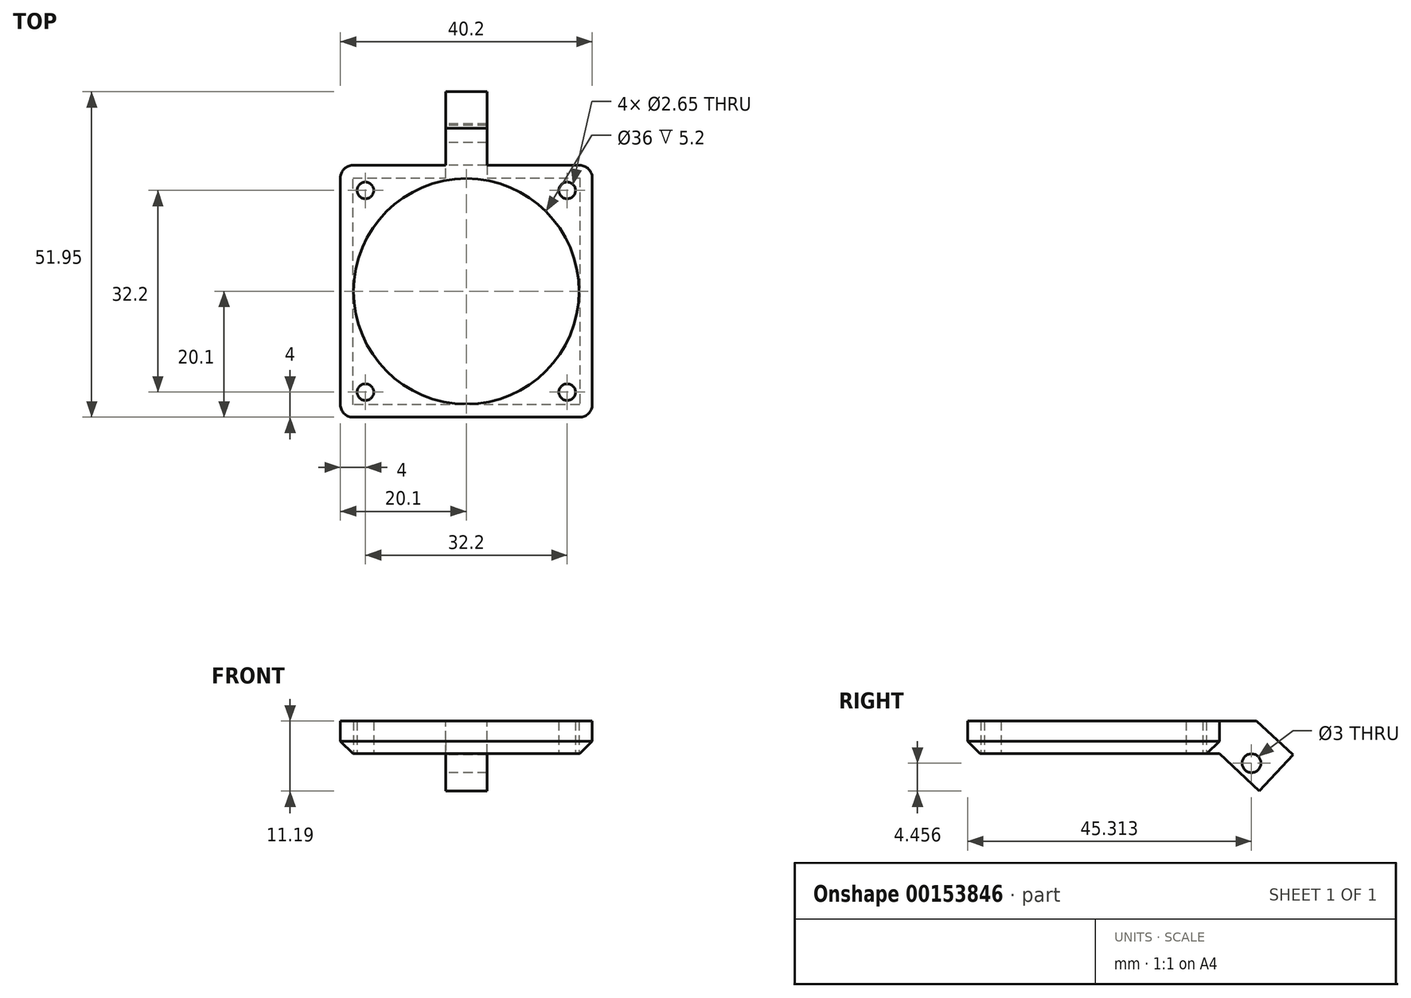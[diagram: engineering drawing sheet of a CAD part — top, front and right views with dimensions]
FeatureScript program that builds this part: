
annotation { "Feature Type Name" : "Feature", "Feature Type Description" : "" }
export const myFeature = defineFeature(function(context is Context, id is Id, definition is map)
    precondition{}
    {
        {
            var Q0;
            Q0=qCreatedBy(makeId("Top.planeOp"),FACE);
            var sketch = newSketch(context, id + "F0", { "sketchPlane" : qUnion([Q0])});
            skLineSegment(sketch, "E0.bottom", {"start": v(20.1, -20.1) * mm, "end": v(-20.1, -20.1) * mm});
            skLineSegment(sketch, "E0.top", {"start": v(20.1, 20.1) * mm, "end": v(-20.1, 20.1) * mm});
            skLineSegment(sketch, "E0.left", {"start": v(20.1, -20.1) * mm, "end": v(20.1, 20.1) * mm});
            skLineSegment(sketch, "E0.right", {"start": v(-20.1, -20.1) * mm, "end": v(-20.1, 20.1) * mm});
            skPoint(sketch, "E0.middle", {"position": v(0, 0) * mm});
            skLineSegment(sketch, "E1.bottom", {"start": v(-20.1, 20.1) * mm, "end": v(-16.1, 20.1) * mm, "construction": true});
            skLineSegment(sketch, "E1.top", {"start": v(-20.1, 16.1) * mm, "end": v(-16.1, 16.1) * mm, "construction": true});
            skLineSegment(sketch, "E1.left", {"start": v(-20.1, 20.1) * mm, "end": v(-20.1, 16.1) * mm, "construction": true});
            skLineSegment(sketch, "E1.right", {"start": v(-16.1, 20.1) * mm, "end": v(-16.1, 16.1) * mm, "construction": true});
            skCircle(sketch, "E2", {"center": v(-16.1, 16.1) * mm, "radius": 1.32 * mm});
            skCircle(sketch, "E3.1.0.0", {"center": v(16.1, 16.1) * mm, "radius": 1.32 * mm});
            skLineSegment(sketch, "E3.direction1", {"start": v(-16.1, 16.1) * mm, "end": v(16.1, 16.1) * mm, "construction": true});
            skLineSegment(sketch, "E4.MirrorCS", {"start": v(-20.1, -20.1) * mm, "end": v(-16.1, -20.1) * mm, "construction": true});
            skLineSegment(sketch, "E5.MirrorCS", {"start": v(-20.1, -16.1) * mm, "end": v(-16.1, -16.1) * mm, "construction": true});
            skLineSegment(sketch, "E6.MirrorCS", {"start": v(-16.1, -20.1) * mm, "end": v(-16.1, -16.1) * mm, "construction": true});
            skLineSegment(sketch, "E7.MirrorCS", {"start": v(-20.1, -20.1) * mm, "end": v(-20.1, -16.1) * mm, "construction": true});
            skLineSegment(sketch, "E8.MirrorCS", {"start": v(-16.1, -16.1) * mm, "end": v(16.1, -16.1) * mm, "construction": true});
            skCircle(sketch, "E9.MirrorC", {"center": v(-16.1, -16.1) * mm, "radius": 1.32 * mm});
            skCircle(sketch, "E10.MirrorC", {"center": v(16.1, -16.1) * mm, "radius": 1.32 * mm});
            skCircle(sketch, "E11", {"center": v(0, 0) * mm, "radius": 18 * mm});
            skCircle(sketch, "E12", {"center": v(6.17, 0) * mm, "radius": 0.24 * mm});
            skSolve(sketch);
        }
        {
            var Q0;
            Q0=makeQuery(id+"F0.imprint","IMPRINT",FACE,{"disambiguationData":[TD([[makeQuery(id+"F0.imprint","IMPRINT",EDGE,{"derivedFrom":sQuery(id+"F0.wireOp",EDGE,"E0.top")}),1.0]])]});
            extrude(context, id + "F1", {"entities" : qUnion([Q0]), "depth" : 5.2 * mm});
        }
        {
            var Q0;
            Q0=makeQuery(id+"F1.opExtrude","SWEPT_EDGE",EDGE,{"disambiguationData":[OSD([sQuery(id+"F0.wireOp",EDGE,"E0.top"),sQuery(id+"F0.wireOp",EDGE,"E0.right")])]});
            var Q1;
            Q1=makeQuery(id+"F1.opExtrude","SWEPT_EDGE",EDGE,{"disambiguationData":[OSD([sQuery(id+"F0.wireOp",EDGE,"E0.top"),sQuery(id+"F0.wireOp",EDGE,"E0.left")])]});
            var Q2;
            Q2=makeQuery(id+"F1.opExtrude","SWEPT_EDGE",EDGE,{"disambiguationData":[OSD([sQuery(id+"F0.wireOp",EDGE,"E0.left"),sQuery(id+"F0.wireOp",EDGE,"E0.bottom")])]});
            var Q3;
            Q3=makeQuery(id+"F1.opExtrude","SWEPT_EDGE",EDGE,{"disambiguationData":[OSD([sQuery(id+"F0.wireOp",EDGE,"E0.right"),sQuery(id+"F0.wireOp",EDGE,"E0.bottom")])]});
            fillet(context, id + "F2", {"entities" : qUnion([Q0, Q1, Q2, Q3]), "radius" : 2 * mm, "tangentPropagation" : true, "allowEdgeOverflow" : false});
        }
        {
            var Q0;
            Q0=makeQuery(id+"F1.opExtrude","SWEPT_FACE",FACE,{"disambiguationData":[OSD([sQuery(id+"F0.wireOp",EDGE,"E0.top")])]});
            var sketch = newSketch(context, id + "F3", { "sketchPlane" : qUnion([Q0])});
            skLineSegment(sketch, "E13", {"start": v(0, 0) * mm, "end": v(0, 5.2) * mm, "construction": true});
            skSolve(sketch);
        }
        {
            var Q0;
            Q0=sQuery(id+"F3.wireOp",EDGE,"E13");
            cPlane(context, id + "F4", {"entities" : qUnion([Q0]), "cplaneType" : CPlaneType.LINE_ANGLE, "offset" : 25 * mm, "angle" : 0 * degree, "width" : 150 * mm, "height" : 150 * mm});
        }
        {
            var Q0;
            Q0=qCreatedBy(id+"F4.planeOp",FACE);
            var sketch = newSketch(context, id + "F5", { "sketchPlane" : qUnion([Q0])});
            skLineSegment(sketch, "E14.0", {"start": v(20.1, 0) * mm, "end": v(20.1, 5.2) * mm});
            skLineSegment(sketch, "E15.top", {"start": v(31.85, -0.16) * mm, "end": v(26, 5.2) * mm});
            skLineSegment(sketch, "E16.0", {"start": v(-18, 5.2) * mm, "end": v(18, 5.2) * mm});
            skLineSegment(sketch, "E17", {"start": v(20.1, 5.2) * mm, "end": v(18, 5.2) * mm});
            skPoint(sketch, "E18", {"position": v(28.93, 2.52) * mm});
            skLineSegment(sketch, "E19", {"start": v(28.93, 2.52) * mm, "end": v(25.21, -1.53) * mm});
            skCircle(sketch, "E20", {"center": v(25.21, -1.53) * mm, "radius": 1.5 * mm});
            skLineSegment(sketch, "E21", {"start": v(31.85, -0.16) * mm, "end": v(25.21, -1.53) * mm, "construction": true});
            skLineSegment(sketch, "E22", {"start": v(31.85, -0.16) * mm, "end": v(26.45, -6) * mm});
            skLineSegment(sketch, "E23", {"start": v(26.45, -6) * mm, "end": v(20.1, 0) * mm});
            skLineSegment(sketch, "E24", {"start": v(26, 5.2) * mm, "end": v(20.1, 5.2) * mm});
            skSolve(sketch);
        }
        {
            var Q0;
            Q0=makeQuery(id+"F5.imprint","IMPRINT",FACE,{"disambiguationData":[TD([[makeQuery(id+"F5.imprint","IMPRINT",EDGE,{"derivedFrom":sQuery(id+"F5.wireOp",EDGE,"E14.0")}),-1.0]])]});
            extrude(context, id + "F6", {"entities" : qUnion([Q0]), "operationType" : NewBodyOperationType.ADD, "endBound" : BoundingType.SYMMETRIC, "depth" : 6.6 * mm});
        }
        {
            var Q0;
            Q0=makeQuery(id+"F1.opExtrude","CAP_EDGE",EDGE,{"disambiguationData":[OSD([sQuery(id+"F0.wireOp",EDGE,"E0.bottom")])],"isStart":true});
            chamfer(context, id + "F7", {"entities" : qUnion([Q0]), "width" : 2 * mm, "tangentPropagation" : true});
        }
    });
